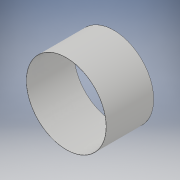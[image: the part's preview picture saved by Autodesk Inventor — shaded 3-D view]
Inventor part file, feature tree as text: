
AUTODESK INVENTOR PART (.ipt)
format: ipt  version: 2019 (Build 230136000, 136)  size: 103,424 bytes
history: native  units: mm
features: extrude x2, sketch x2
ambient origin geometry x8: Origin, YZ Plane, XZ Plane, XY Plane, X Axis, Y Axis, Z Axis, Center Point
bodies: Solid1 (feature_tree)
feature tree (4):
  extrude  "Extrusion1"  Depth=11.9mm TaperAngle=0.0deg
  extrude  "Extrusion2"  Depth=11.9mm TaperAngle=0.0deg
  sketch  "Sketch1"  dims[d0=20.07mm d1=11.9mm d2=0.0mm]
  sketch  "Sketch2"  dims[d3=19.97mm d4=11.9mm d5=0.0mm]
